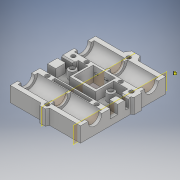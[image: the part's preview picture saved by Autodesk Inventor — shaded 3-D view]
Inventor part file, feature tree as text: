
AUTODESK INVENTOR PART (.ipt)
format: ipt  version: 2018 (Build 220112000, 112)  size: 453,120 bytes
history: native  units: mm
features: extrude x11, sketch x11, chamfer x3, plane x2, mirror x2, hole x1, fillet x1
ambient origin geometry x8: Origin, YZ Plane, XZ Plane, XY Plane, X Axis, Y Axis, Z Axis, Center Point
bodies: Solid1 (feature_tree)
feature tree (31):
  extrude  "Extrusion1"  Depth=68.0mm
  extrude  "Extrusion2"  Depth=22.5mm
  plane  "Work Plane1"
  extrude  "Extrusion3"  Depth=11.0mm
  plane  "Work Plane2"
  mirror  "Mirror1"
  extrude  "Extrusion4"  Depth=15.7mm
  extrude  "Extrusion7"  [1 undecoded]
  chamfer  "Chamfer2"  Distance=24.5mm
  hole  "Hole1"  [1 undecoded]
  mirror  "Mirror3"
  extrude  "Extrusion8"  Depth=7.5mm
  chamfer  "Chamfer3"  Distance=10.0mm
  extrude  "Extrusion9"  Depth=2.5mm
  chamfer  "Chamfer4"  Distance=10.0mm
  extrude  "Extrusion10"  Depth=2.5mm
  fillet  "Fillet2"  Radius=2.3mm
  extrude  "Extrusion11"  Depth=6.0mm
  extrude  "Extrusion12"  Depth=2.5mm
  sketch  "Sketch14"  dims[d61=10.0mm d62=10.0mm d54=3.6mm d55=6.0mm d56=4.0mm d57=2.0mm d58=90.0deg d59=8.0mm d60=20.594885mm d64=2.3mm d66=10.0mm d67=3.0mm d68=2.3mm d70=6.0mm d73=3.0mm d75=5.0mm d77=10.0mm d78=0.0mm d79=1.5mm d80=2.0mm d81=45.0deg d82=2.0mm d83=1.5mm d84=1.5mm d93=10.0mm d94=0.0mm d95=1.0mm d96=2.0mm d97=45.0deg d99=11.7mm d100=4.325mm d101=3.0mm d102=6.5mm d103=1.6mm d105=15.3mm d106=1.525mm d107=6.9mm d108=2.6mm d109=0.95mm d110=5.05mm d111=2.6mm d112=0.61mm d113=0.0mm d114=0.3mm d116=2.6mm d117=30.0mm d118=4.65mm d119=3.3mm d121=3.3mm d122=4.65mm d123=3.3mm d124=3.3mm d125=3.3mm d126=0.5mm d127=0.0mm d128=0.0mm d131=1.749395mm d133=7.0mm d134=0.0mm d138=6.0mm d139=6.0mm d140=6.0mm d141=6.0mm d142=10.0mm d150=2.5mm d151=0.0mm d152=0.651024mm]
  extrude  "Extrusion13"  Depth=2.5mm
  sketch  "Sketch1"  dims[d0=56.0mm d1=68.0mm]
  sketch  "Sketch2"  dims[d2=12.0mm d3=0.0mm d4=22.5mm]
  sketch  "Sketch3"  dims[d5=11.0mm d6=11.0mm]
  sketch  "Sketch4"  dims[d7=0.0mm d8=0.0mm d9=15.7mm]
  sketch  "Sketch7"  dims[d10=15.7mm d11=-2.5mm d12=24.5mm d13=0.0mm]
  sketch  "Sketch9"  dims[d14=-28.0mm d17=7.0mm d18=0.0mm]
  sketch  "Sketch10"  dims[d21=1.6mm d44=7.5mm]
  sketch  "Sketch11"  dims[d45=12.6mm]
  sketch  "Sketch12"  dims[d46=6.0mm d47=10.0mm d48=0.0mm]
  sketch  "Sketch13"  dims[d49=0.9mm d50=2.0mm d51=45.0deg]
note: 2 required parameter values undecoded (feature->parameter linkage not recoverable at this tier; creation-order binding heuristic only, values carry confidence <= 0.55)
